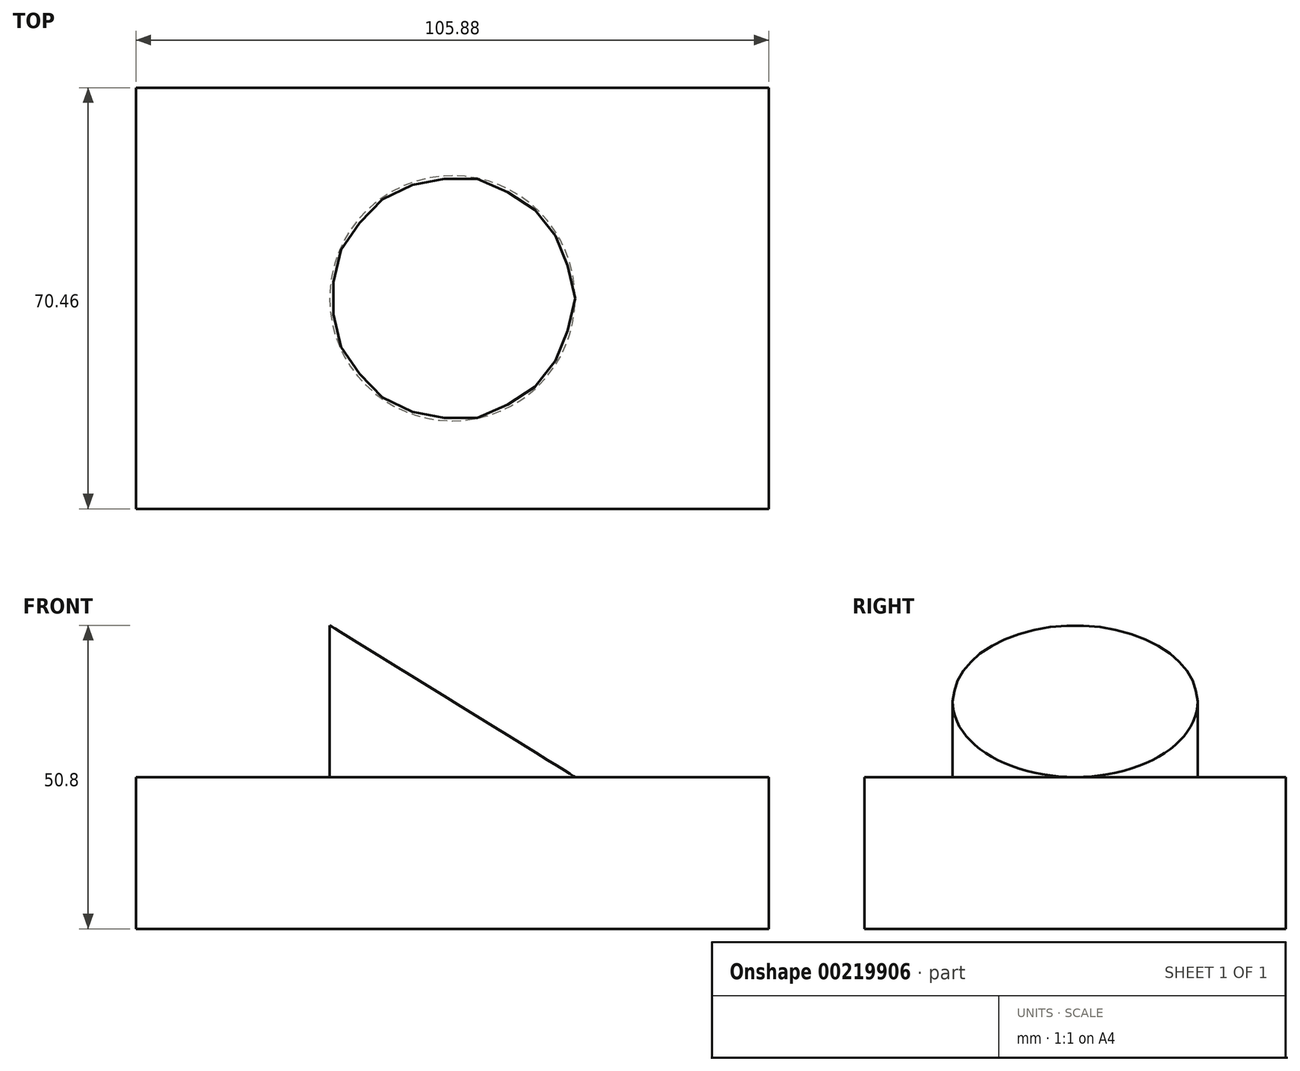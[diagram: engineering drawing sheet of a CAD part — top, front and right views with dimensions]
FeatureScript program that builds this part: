
annotation { "Feature Type Name" : "Feature", "Feature Type Description" : "" }
export const myFeature = defineFeature(function(context is Context, id is Id, definition is map)
    precondition{}
    {
        {
            var Q0;
            Q0=qCreatedBy(makeId("Top.planeOp"),FACE);
            var sketch = newSketch(context, id + "F0", { "sketchPlane" : qUnion([Q0])});
            skLineSegment(sketch, "E0.bottom", {"start": v(52.94, 35.23) * mm, "end": v(-52.94, 35.23) * mm});
            skLineSegment(sketch, "E0.top", {"start": v(52.94, -35.23) * mm, "end": v(-52.94, -35.23) * mm});
            skLineSegment(sketch, "E0.left", {"start": v(52.94, 35.23) * mm, "end": v(52.94, -35.23) * mm});
            skLineSegment(sketch, "E0.right", {"start": v(-52.94, 35.23) * mm, "end": v(-52.94, -35.23) * mm});
            skPoint(sketch, "E0.middle", {"position": v(0, 0) * mm});
            skSolve(sketch);
        }
        {
            var Q0;
            Q0=makeQuery(id+"F0.imprint","IMPRINT",FACE,{"disambiguationData":[TD([[makeQuery(id+"F0.imprint","IMPRINT",EDGE,{"derivedFrom":sQuery(id+"F0.wireOp",EDGE,"E0.bottom")}),1.0]])]});
            extrude(context, id + "F1", {"entities" : qUnion([Q0]), "depth" : 25.4 * mm});
        }
        {
            var Q0;
            Q0=makeQuery(id+"F1.opExtrude","CAP_FACE",FACE,{"disambiguationData":[OSD([sQuery(id+"F0.wireOp",EDGE,"E0.bottom"),sQuery(id+"F0.wireOp",EDGE,"E0.top"),sQuery(id+"F0.wireOp",EDGE,"E0.left"),sQuery(id+"F0.wireOp",EDGE,"E0.right")])],"isStart":false});
            var sketch = newSketch(context, id + "F2", { "sketchPlane" : qUnion([Q0])});
            skCircle(sketch, "E1", {"center": v(0, 0) * mm, "radius": 20.52 * mm});
            skSolve(sketch);
        }
        {
            var Q0;
            Q0=makeQuery(id+"F2.imprint","IMPRINT",FACE,{"disambiguationData":[TD([[makeQuery(id+"F2.imprint","IMPRINT",EDGE,{"derivedFrom":sQuery(id+"F2.wireOp",EDGE,"E1")}),1.0]])]});
            extrude(context, id + "F3", {"entities" : qUnion([Q0]), "operationType" : NewBodyOperationType.ADD, "depth" : 25.4 * mm});
        }
        {
            var Q0;
            Q0=qCreatedBy(makeId("Front.planeOp"),FACE);
            var sketch = newSketch(context, id + "F4", { "sketchPlane" : qUnion([Q0])});
            skLineSegment(sketch, "E2.0", {"start": v(-20.52, 50.8) * mm, "end": v(20.52, 50.8) * mm});
            skLineSegment(sketch, "E3", {"start": v(20.52, 50.8) * mm, "end": v(20.52, 25.4) * mm});
            skLineSegment(sketch, "E4", {"start": v(-20.52, 50.8) * mm, "end": v(20.52, 25.4) * mm});
            skSolve(sketch);
        }
        {
            var Q0;
            Q0 = qSketchRegion(id + "F4", true);
            extrude(context, id + "F5", {"entities" : qUnion([Q0]), "operationType" : NewBodyOperationType.REMOVE, "endBound" : BoundingType.THROUGH_ALL, "oppositeDirection" : true, "depth" : 25.4 * mm, "hasSecondDirection" : true, "secondDirectionBound" : SecondDirectionBoundingType.THROUGH_ALL, "secondDirectionOppositeDirection" : false, "secondDirectionDepth" : 25.4 * mm});
        }
    });
